# Revit family: Shower-Showerhead-KOHLER-FINIAL-K-10282T_1
name_source: partatom
category: Plumbing Fixtures
revit_build: Autodesk Revit 2017 (Build: 20160225_1515(x64)
units: mm (PartAtom-declared; Revit-internal decimal feet)

## family parameters
Cut with Voids When Loaded = No
Host = Face
OmniClass Number = 23.31.17.00
OmniClass Title = Showers
Part Type = Normal
Room Calculation Point = No
Round Connector Dimension = Use Diameter
Shared = No

## types (5) — shared parameters
ADA Compliant = No
Assembly Code = D2010700
CW Connection = No
Cold Water Inlet = Cold Water Inlet
Date Modified = 06/24/2020
Default Elevation = 0"
Drain Included = No
Flow Rate = 0 GPM
HW Connection = Yes
Height = 4 11/16"
Hot Water Inlet = Hot Water Inlet
Length = 5 1/2"
Manufacturer = KOHLER Co.
Master Format 2014 = 22 42 23
Master Format 2014 Name = Residential Showers
Material = Premium Metal Construction
Panel Thickness = 0"
Pressure = 72.52 psi
Product Documentation Link = https://files.kohler.com.cn
Product Name = FINIAL
Product Page URL = https://www.kohler.com.cn
Tempered Water Inlet = Tempered Water Inlet
URL = http://www.kohler.com.cn
Vent Connection = No
Waste Connection = No
Waste Water Outlet = Waste Water Outlet
WaterSense Certified = No
Width = 5 1/2"

## per-type parameters (varying)
| type | Description | Finish | Model | Type |
| CP-Polished Chrome | Rain shower 5.5 | Kohler-Metal-CP-Polished_Chrome | K-10282T-AK-CP | 1 |
| AF-Flange Gold | Rain shower 5.5 | Kohler-Metal-AF-Flange_Gold | K-10282T-AK-AF | 2 |
| BN-Roman Silver | Rain shower 5.5 | Kohler-Metal-BN-Roman_Silver | K-10282T-AK-BN | 3 |
| SN-Champagne Gold | Rain shower 5.5 | Kohler-Metal-SN-Champagne_Gold | K-10282T-AK-SN | 4 |
| Flow Regulator,CP-Polished Chrome | Shower 5.5 | Kohler-Metal-CP-Polished_Chrome | K-10282T-E2-CP | 5 |

## geometry (parser evidence)
native form markers: Sweep x5
no freeform markers — native parametric forms only
